# Revit family: WGH
name_source: partatom
category: Lighting Fixtures
revit_build: Autodesk Revit Architecture 2012 (Build: 20110309_2315(x64)
units: mm (PartAtom-declared; Revit-internal decimal feet)

## types (1)
- WGH- Medium- BR
    Color Filter = 16777215
    Colour = Dark bronze powder paint
    Default Elevation = 48"
    Description = Perimeter lighting for safety and security. 
Use on factories, warehouses, self storage , commercial buildings etc.
    Dimming Lamp Color Temperature Shift = <None>
    Emit from Line Length = 6"
    Glass = Glass
    Lamp = 1
    Light Source Symbol Size = 3"
    Light source = 0 lx
    Manufacturer = Hubbell outdoor lighting
    Manufacturer Fax = (864)-678-1065
    Model = WGH
    Product Documentation Link = http://www.hubbelloutdoor.com
    Product Page URL = http://www.hubbelloutdoor.com
    URL = http://www.hubbelloutdoor.com
    Wattage Comments = 100W/100W

## geometry (parser evidence)
native form markers: Blend x2, Sweep x1
no freeform markers — native parametric forms only
